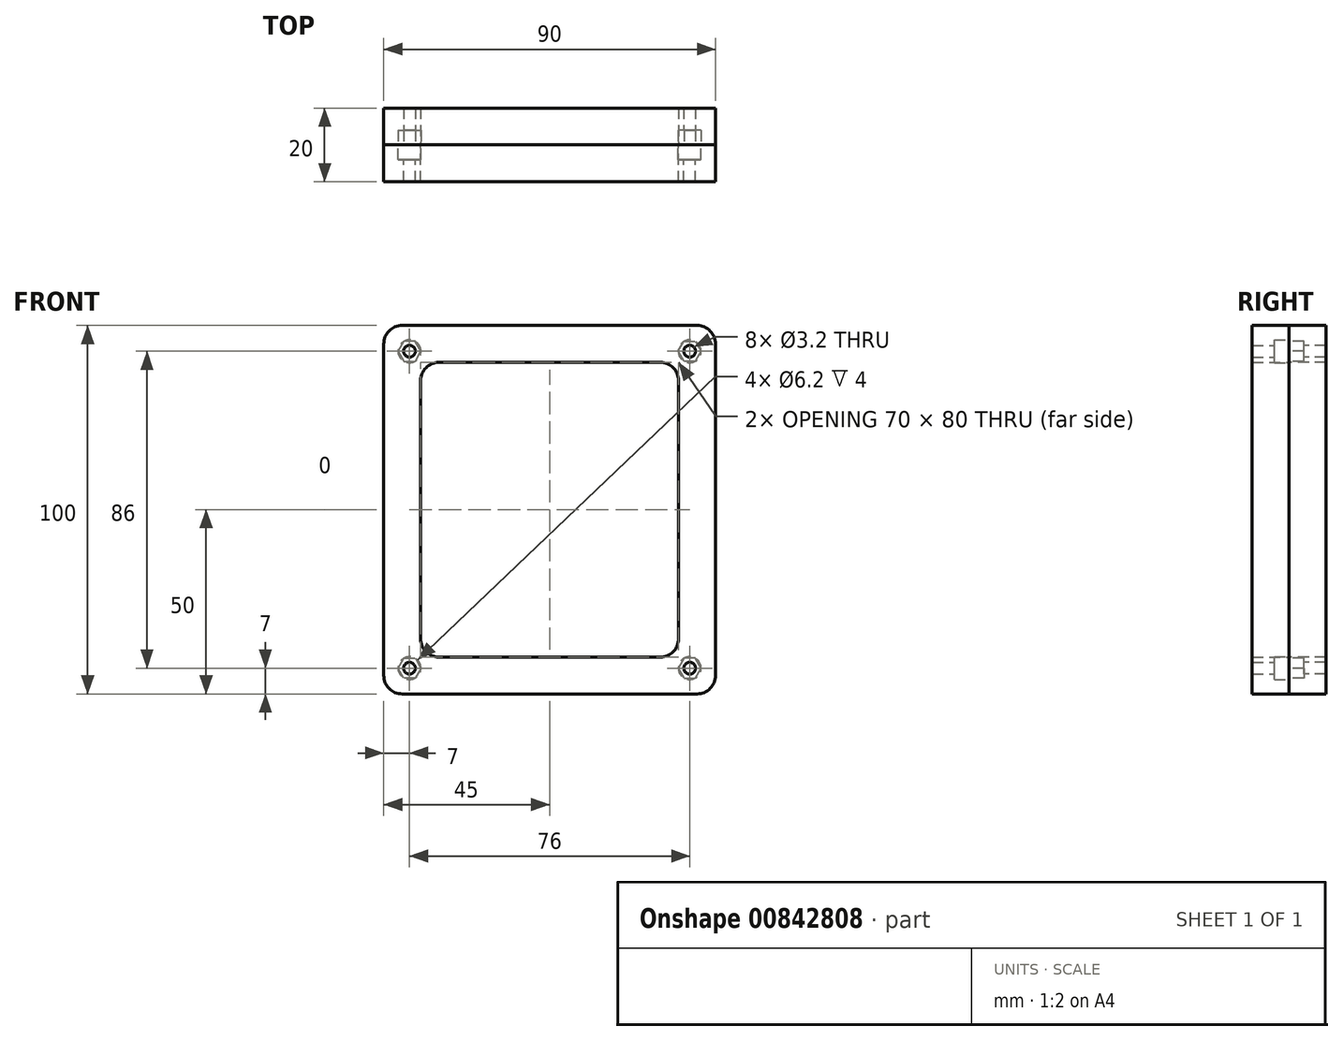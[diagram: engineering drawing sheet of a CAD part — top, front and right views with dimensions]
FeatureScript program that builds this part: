
annotation { "Feature Type Name" : "Feature", "Feature Type Description" : "" }
export const myFeature = defineFeature(function(context is Context, id is Id, definition is map)
    precondition{}
    {
        {
            var Q0;
            Q0=qCreatedBy(makeId("Front.planeOp"),FACE);
            var sketch = newSketch(context, id + "F0", { "sketchPlane" : qUnion([Q0])});
            skLineSegment(sketch, "E0.bottom", {"start": v(30, -40) * mm, "end": v(-30, -40) * mm});
            skLineSegment(sketch, "E0.top", {"start": v(30, 40) * mm, "end": v(-30, 40) * mm});
            skLineSegment(sketch, "E0.left", {"start": v(35, -35) * mm, "end": v(35, 35) * mm});
            skLineSegment(sketch, "E0.right", {"start": v(-35, -35) * mm, "end": v(-35, 35) * mm});
            skPoint(sketch, "E0.middle", {"position": v(0, 0) * mm});
            skLineSegment(sketch, "E1.bottom", {"start": v(40, -50) * mm, "end": v(-40, -50) * mm});
            skLineSegment(sketch, "E1.top", {"start": v(40, 50) * mm, "end": v(-40, 50) * mm});
            skLineSegment(sketch, "E1.left", {"start": v(45, -45) * mm, "end": v(45, 45) * mm});
            skLineSegment(sketch, "E1.right", {"start": v(-45, -45) * mm, "end": v(-45, 45) * mm});
            skLineSegment(sketch, "E2.bottom", {"start": v(10, 65) * mm, "end": v(-10, 65) * mm});
            skLineSegment(sketch, "E2.top", {"start": v(10, 75) * mm, "end": v(-10, 75) * mm});
            skLineSegment(sketch, "E2.left", {"start": v(10, 65) * mm, "end": v(10, 75) * mm});
            skLineSegment(sketch, "E2.right", {"start": v(-10, 65) * mm, "end": v(-10, 75) * mm});
            skPoint(sketch, "E2.middle", {"position": v(0, 70) * mm});
            skLineSegment(sketch, "E3", {"start": v(0, 26.34) * mm, "end": v(0, -22.9) * mm, "construction": true});
            skLineSegment(sketch, "E4", {"start": v(-20.89, 0) * mm, "end": v(22.35, 0) * mm, "construction": true});
            skCircle(sketch, "E5", {"center": v(38, 43) * mm, "radius": 1.6 * mm});
            skCircle(sketch, "E6", {"center": v(38, 43) * mm, "radius": 3.1 * mm});
            skCircle(sketch, "E7.cCircle", {"center": v(38, 43) * mm, "radius": 3.1 * mm, "construction": true});
            skLineSegment(sketch, "E7.0", {"start": v(39.55, 40.32) * mm, "end": v(36.45, 40.32) * mm});
            skLineSegment(sketch, "E7.1", {"start": v(36.45, 40.32) * mm, "end": v(34.9, 43) * mm});
            skLineSegment(sketch, "E7.2", {"start": v(34.9, 43) * mm, "end": v(36.45, 45.68) * mm});
            skLineSegment(sketch, "E7.3", {"start": v(36.45, 45.68) * mm, "end": v(39.55, 45.68) * mm});
            skLineSegment(sketch, "E7.4", {"start": v(39.55, 45.68) * mm, "end": v(41.1, 43) * mm});
            skLineSegment(sketch, "E7.5", {"start": v(41.1, 43) * mm, "end": v(39.55, 40.32) * mm});
            skLineSegment(sketch, "E8.MirrorCS", {"start": v(-34.9, 43) * mm, "end": v(-36.45, 45.68) * mm});
            skLineSegment(sketch, "E9.MirrorCS", {"start": v(-39.55, 45.68) * mm, "end": v(-41.1, 43) * mm});
            skLineSegment(sketch, "E10.MirrorCS", {"start": v(-36.45, 40.32) * mm, "end": v(-34.9, 43) * mm});
            skLineSegment(sketch, "E11.MirrorCS", {"start": v(-41.1, 43) * mm, "end": v(-39.55, 40.32) * mm});
            skLineSegment(sketch, "E12.MirrorCS", {"start": v(-36.45, 45.68) * mm, "end": v(-39.55, 45.68) * mm});
            skCircle(sketch, "E13.MirrorC", {"center": v(-38, 43) * mm, "radius": 3.1 * mm});
            skLineSegment(sketch, "E14.MirrorCS", {"start": v(-39.55, 40.32) * mm, "end": v(-36.45, 40.32) * mm});
            skCircle(sketch, "E15.MirrorC", {"center": v(-38, 43) * mm, "radius": 3.1 * mm, "construction": true});
            skCircle(sketch, "E16.MirrorC", {"center": v(-38, 43) * mm, "radius": 1.6 * mm});
            skLineSegment(sketch, "E17.MirrorCS", {"start": v(-36.45, -40.32) * mm, "end": v(-34.9, -43) * mm});
            skLineSegment(sketch, "E18.MirrorCS", {"start": v(-34.9, -43) * mm, "end": v(-36.45, -45.68) * mm});
            skLineSegment(sketch, "E19.MirrorCS", {"start": v(-39.55, -45.68) * mm, "end": v(-41.1, -43) * mm});
            skLineSegment(sketch, "E20.MirrorCS", {"start": v(-39.55, -40.32) * mm, "end": v(-36.45, -40.32) * mm});
            skLineSegment(sketch, "E21.MirrorCS", {"start": v(-41.1, -43) * mm, "end": v(-39.55, -40.32) * mm});
            skCircle(sketch, "E22.MirrorC", {"center": v(-38, -43) * mm, "radius": 3.1 * mm});
            skCircle(sketch, "E23.MirrorC", {"center": v(-38, -43) * mm, "radius": 3.1 * mm, "construction": true});
            skLineSegment(sketch, "E24.MirrorCS", {"start": v(-36.45, -45.68) * mm, "end": v(-39.55, -45.68) * mm});
            skCircle(sketch, "E25.MirrorC", {"center": v(-38, -43) * mm, "radius": 1.6 * mm});
            skLineSegment(sketch, "E26.MirrorCS", {"start": v(39.55, -40.32) * mm, "end": v(36.45, -40.32) * mm});
            skLineSegment(sketch, "E27.MirrorCS", {"start": v(36.45, -40.32) * mm, "end": v(34.9, -43) * mm});
            skLineSegment(sketch, "E28.MirrorCS", {"start": v(34.9, -43) * mm, "end": v(36.45, -45.68) * mm});
            skLineSegment(sketch, "E29.MirrorCS", {"start": v(36.45, -45.68) * mm, "end": v(39.55, -45.68) * mm});
            skLineSegment(sketch, "E30.MirrorCS", {"start": v(41.1, -43) * mm, "end": v(39.55, -40.32) * mm});
            skLineSegment(sketch, "E31.MirrorCS", {"start": v(39.55, -45.68) * mm, "end": v(41.1, -43) * mm});
            skCircle(sketch, "E32.MirrorC", {"center": v(38, -43) * mm, "radius": 3.1 * mm});
            skCircle(sketch, "E33.MirrorC", {"center": v(38, -43) * mm, "radius": 1.6 * mm});
            skCircle(sketch, "E34.MirrorC", {"center": v(38, -43) * mm, "radius": 3.1 * mm, "construction": true});
            skPoint(sketch, "E35.visualSharp", {"position": v(-35, 40) * mm});
            skArc(sketch, "E35.filletArc", {"start": v(-30, 40) * mm, "mid": v(-33.54, 38.54) * mm, "end": v(-35, 35) * mm});
            skPoint(sketch, "E36.visualSharp", {"position": v(35, 40) * mm});
            skArc(sketch, "E36.filletArc", {"start": v(35, 35) * mm, "mid": v(33.54, 38.54) * mm, "end": v(30, 40) * mm});
            skPoint(sketch, "E37.visualSharp", {"position": v(35, -40) * mm});
            skArc(sketch, "E37.filletArc", {"start": v(30, -40) * mm, "mid": v(33.54, -38.54) * mm, "end": v(35, -35) * mm});
            skPoint(sketch, "E38.visualSharp", {"position": v(-35, -40) * mm});
            skArc(sketch, "E38.filletArc", {"start": v(-35, -35) * mm, "mid": v(-33.54, -38.54) * mm, "end": v(-30, -40) * mm});
            skPoint(sketch, "E39.visualSharp", {"position": v(45, 50) * mm});
            skArc(sketch, "E39.filletArc", {"start": v(45, 45) * mm, "mid": v(43.54, 48.54) * mm, "end": v(40, 50) * mm});
            skPoint(sketch, "E40.visualSharp", {"position": v(-45, 50) * mm});
            skArc(sketch, "E40.filletArc", {"start": v(-40, 50) * mm, "mid": v(-43.54, 48.54) * mm, "end": v(-45, 45) * mm});
            skPoint(sketch, "E41.visualSharp", {"position": v(-45, -50) * mm});
            skArc(sketch, "E41.filletArc", {"start": v(-45, -45) * mm, "mid": v(-43.54, -48.54) * mm, "end": v(-40, -50) * mm});
            skPoint(sketch, "E42.visualSharp", {"position": v(45, -50) * mm});
            skArc(sketch, "E42.filletArc", {"start": v(40, -50) * mm, "mid": v(43.54, -48.54) * mm, "end": v(45, -45) * mm});
            skSolve(sketch);
        }
        {
            var Q0;
            Q0=makeQuery(id+"F0.imprint","IMPRINT",FACE,{"disambiguationData":[TD([[makeQuery(id+"F0.imprint","IMPRINT",EDGE,{"derivedFrom":sQuery(id+"F0.wireOp",EDGE,"E0.bottom")}),1.0]])]});
            var Q1;
            {var subQ0=sQuery(id+"F0.wireOp",EDGE,"E10.MirrorCS");Q1=makeQuery(id+"F0.imprint","IMPRINT",FACE,{"disambiguationData":[TD([[makeQuery(id+"F0.imprint","IMPRINT",EDGE,{"derivedFrom":subQ0}),-1.0]])]});}
            var Q2;
            Q2=makeQuery(id+"F0.imprint","IMPRINT",FACE,{"disambiguationData":[TD([[makeQuery(id+"F0.imprint","IMPRINT",EDGE,{"derivedFrom":sQuery(id+"F0.wireOp",EDGE,"E8.MirrorCS")}),1.0]])]});
            var Q3;
            {var subQ0=sQuery(id+"F0.wireOp",EDGE,"E8.MirrorCS");Q3=makeQuery(id+"F0.imprint","IMPRINT",FACE,{"disambiguationData":[TD([[makeQuery(id+"F0.imprint","IMPRINT",EDGE,{"derivedFrom":subQ0}),-1.0]])]});}
            var Q4;
            {var subQ0=sQuery(id+"F0.wireOp",EDGE,"E12.MirrorCS");Q4=makeQuery(id+"F0.imprint","IMPRINT",FACE,{"disambiguationData":[TD([[makeQuery(id+"F0.imprint","IMPRINT",EDGE,{"derivedFrom":subQ0}),-1.0]])]});}
            var Q5;
            {var subQ0=sQuery(id+"F0.wireOp",EDGE,"E9.MirrorCS");Q5=makeQuery(id+"F0.imprint","IMPRINT",FACE,{"disambiguationData":[TD([[makeQuery(id+"F0.imprint","IMPRINT",EDGE,{"derivedFrom":subQ0}),-1.0]])]});}
            var Q6;
            {var subQ0=sQuery(id+"F0.wireOp",EDGE,"E11.MirrorCS");Q6=makeQuery(id+"F0.imprint","IMPRINT",FACE,{"disambiguationData":[TD([[makeQuery(id+"F0.imprint","IMPRINT",EDGE,{"derivedFrom":subQ0}),-1.0]])]});}
            var Q7;
            {var subQ0=sQuery(id+"F0.wireOp",EDGE,"E14.MirrorCS");Q7=makeQuery(id+"F0.imprint","IMPRINT",FACE,{"disambiguationData":[TD([[makeQuery(id+"F0.imprint","IMPRINT",EDGE,{"derivedFrom":subQ0}),-1.0]])]});}
            var Q8;
            {var subQ0=sQuery(id+"F0.wireOp",EDGE,"E7.4");Q8=makeQuery(id+"F0.imprint","IMPRINT",FACE,{"disambiguationData":[TD([[makeQuery(id+"F0.imprint","IMPRINT",EDGE,{"derivedFrom":subQ0}),1.0]])]});}
            var Q9;
            Q9=makeQuery(id+"F0.imprint","IMPRINT",FACE,{"disambiguationData":[TD([[makeQuery(id+"F0.imprint","IMPRINT",EDGE,{"derivedFrom":sQuery(id+"F0.wireOp",EDGE,"E5")}),-1.0]])]});
            var Q10;
            {var subQ0=sQuery(id+"F0.wireOp",EDGE,"E7.1");Q10=makeQuery(id+"F0.imprint","IMPRINT",FACE,{"disambiguationData":[TD([[makeQuery(id+"F0.imprint","IMPRINT",EDGE,{"derivedFrom":subQ0}),1.0]])]});}
            var Q11;
            {var subQ0=sQuery(id+"F0.wireOp",EDGE,"E7.0");Q11=makeQuery(id+"F0.imprint","IMPRINT",FACE,{"disambiguationData":[TD([[makeQuery(id+"F0.imprint","IMPRINT",EDGE,{"derivedFrom":subQ0}),1.0]])]});}
            var Q12;
            {var subQ0=sQuery(id+"F0.wireOp",EDGE,"E7.3");Q12=makeQuery(id+"F0.imprint","IMPRINT",FACE,{"disambiguationData":[TD([[makeQuery(id+"F0.imprint","IMPRINT",EDGE,{"derivedFrom":subQ0}),1.0]])]});}
            var Q13;
            {var subQ0=sQuery(id+"F0.wireOp",EDGE,"E7.5");Q13=makeQuery(id+"F0.imprint","IMPRINT",FACE,{"disambiguationData":[TD([[makeQuery(id+"F0.imprint","IMPRINT",EDGE,{"derivedFrom":subQ0}),1.0]])]});}
            var Q14;
            {var subQ0=sQuery(id+"F0.wireOp",EDGE,"E7.2");Q14=makeQuery(id+"F0.imprint","IMPRINT",FACE,{"disambiguationData":[TD([[makeQuery(id+"F0.imprint","IMPRINT",EDGE,{"derivedFrom":subQ0}),1.0]])]});}
            var Q15;
            Q15=makeQuery(id+"F0.imprint","IMPRINT",FACE,{"disambiguationData":[TD([[makeQuery(id+"F0.imprint","IMPRINT",EDGE,{"derivedFrom":sQuery(id+"F0.wireOp",EDGE,"E26.MirrorCS")}),1.0]])]});
            var Q16;
            {var subQ0=sQuery(id+"F0.wireOp",EDGE,"E31.MirrorCS");Q16=makeQuery(id+"F0.imprint","IMPRINT",FACE,{"disambiguationData":[TD([[makeQuery(id+"F0.imprint","IMPRINT",EDGE,{"derivedFrom":subQ0}),-1.0]])]});}
            var Q17;
            {var subQ0=sQuery(id+"F0.wireOp",EDGE,"E27.MirrorCS");Q17=makeQuery(id+"F0.imprint","IMPRINT",FACE,{"disambiguationData":[TD([[makeQuery(id+"F0.imprint","IMPRINT",EDGE,{"derivedFrom":subQ0}),-1.0]])]});}
            var Q18;
            {var subQ0=sQuery(id+"F0.wireOp",EDGE,"E29.MirrorCS");Q18=makeQuery(id+"F0.imprint","IMPRINT",FACE,{"disambiguationData":[TD([[makeQuery(id+"F0.imprint","IMPRINT",EDGE,{"derivedFrom":subQ0}),-1.0]])]});}
            var Q19;
            {var subQ0=sQuery(id+"F0.wireOp",EDGE,"E28.MirrorCS");Q19=makeQuery(id+"F0.imprint","IMPRINT",FACE,{"disambiguationData":[TD([[makeQuery(id+"F0.imprint","IMPRINT",EDGE,{"derivedFrom":subQ0}),-1.0]])]});}
            var Q20;
            {var subQ0=sQuery(id+"F0.wireOp",EDGE,"E26.MirrorCS");Q20=makeQuery(id+"F0.imprint","IMPRINT",FACE,{"disambiguationData":[TD([[makeQuery(id+"F0.imprint","IMPRINT",EDGE,{"derivedFrom":subQ0}),-1.0]])]});}
            var Q21;
            {var subQ0=sQuery(id+"F0.wireOp",EDGE,"E30.MirrorCS");Q21=makeQuery(id+"F0.imprint","IMPRINT",FACE,{"disambiguationData":[TD([[makeQuery(id+"F0.imprint","IMPRINT",EDGE,{"derivedFrom":subQ0}),-1.0]])]});}
            var Q22;
            Q22=makeQuery(id+"F0.imprint","IMPRINT",FACE,{"disambiguationData":[TD([[makeQuery(id+"F0.imprint","IMPRINT",EDGE,{"derivedFrom":sQuery(id+"F0.wireOp",EDGE,"E17.MirrorCS")}),-1.0]])]});
            var Q23;
            {var subQ0=sQuery(id+"F0.wireOp",EDGE,"E24.MirrorCS");Q23=makeQuery(id+"F0.imprint","IMPRINT",FACE,{"disambiguationData":[TD([[makeQuery(id+"F0.imprint","IMPRINT",EDGE,{"derivedFrom":subQ0}),1.0]])]});}
            var Q24;
            {var subQ0=sQuery(id+"F0.wireOp",EDGE,"E18.MirrorCS");Q24=makeQuery(id+"F0.imprint","IMPRINT",FACE,{"disambiguationData":[TD([[makeQuery(id+"F0.imprint","IMPRINT",EDGE,{"derivedFrom":subQ0}),1.0]])]});}
            var Q25;
            {var subQ0=sQuery(id+"F0.wireOp",EDGE,"E19.MirrorCS");Q25=makeQuery(id+"F0.imprint","IMPRINT",FACE,{"disambiguationData":[TD([[makeQuery(id+"F0.imprint","IMPRINT",EDGE,{"derivedFrom":subQ0}),1.0]])]});}
            var Q26;
            {var subQ0=sQuery(id+"F0.wireOp",EDGE,"E21.MirrorCS");Q26=makeQuery(id+"F0.imprint","IMPRINT",FACE,{"disambiguationData":[TD([[makeQuery(id+"F0.imprint","IMPRINT",EDGE,{"derivedFrom":subQ0}),1.0]])]});}
            var Q27;
            {var subQ0=sQuery(id+"F0.wireOp",EDGE,"E20.MirrorCS");Q27=makeQuery(id+"F0.imprint","IMPRINT",FACE,{"disambiguationData":[TD([[makeQuery(id+"F0.imprint","IMPRINT",EDGE,{"derivedFrom":subQ0}),1.0]])]});}
            var Q28;
            {var subQ0=sQuery(id+"F0.wireOp",EDGE,"E17.MirrorCS");Q28=makeQuery(id+"F0.imprint","IMPRINT",FACE,{"disambiguationData":[TD([[makeQuery(id+"F0.imprint","IMPRINT",EDGE,{"derivedFrom":subQ0}),1.0]])]});}
            extrude(context, id + "F1", {"entities" : qUnion([Q0, Q1, Q2, Q3, Q4, Q5, Q6, Q7, Q8, Q9, Q10, Q11, Q12, Q13, Q14, Q15, Q16, Q17, Q18, Q19, Q20, Q21, Q22, Q23, Q24, Q25, Q26, Q27, Q28]), "depth" : 10 * mm, "offsetDistance" : 25 * mm});
        }
        {
            var Q0;
            Q0=makeQuery(id+"F0.imprint","IMPRINT",FACE,{"disambiguationData":[TD([[makeQuery(id+"F0.imprint","IMPRINT",EDGE,{"derivedFrom":sQuery(id+"F0.wireOp",EDGE,"E26.MirrorCS")}),1.0]])]});
            var Q1;
            Q1=makeQuery(id+"F0.imprint","IMPRINT",FACE,{"disambiguationData":[TD([[makeQuery(id+"F0.imprint","IMPRINT",EDGE,{"derivedFrom":sQuery(id+"F0.wireOp",EDGE,"E0.bottom")}),1.0]])]});
            var Q2;
            Q2=makeQuery(id+"F0.imprint","IMPRINT",FACE,{"disambiguationData":[TD([[makeQuery(id+"F0.imprint","IMPRINT",EDGE,{"derivedFrom":sQuery(id+"F0.wireOp",EDGE,"E17.MirrorCS")}),-1.0]])]});
            var Q3;
            Q3=makeQuery(id+"F0.imprint","IMPRINT",FACE,{"disambiguationData":[TD([[makeQuery(id+"F0.imprint","IMPRINT",EDGE,{"derivedFrom":sQuery(id+"F0.wireOp",EDGE,"E5")}),-1.0]])]});
            var Q4;
            Q4=makeQuery(id+"F0.imprint","IMPRINT",FACE,{"disambiguationData":[TD([[makeQuery(id+"F0.imprint","IMPRINT",EDGE,{"derivedFrom":sQuery(id+"F0.wireOp",EDGE,"E8.MirrorCS")}),1.0]])]});
            var Q5;
            {var subQ0=sQuery(id+"F0.wireOp",EDGE,"E14.MirrorCS");Q5=makeQuery(id+"F0.imprint","IMPRINT",FACE,{"disambiguationData":[TD([[makeQuery(id+"F0.imprint","IMPRINT",EDGE,{"derivedFrom":subQ0}),-1.0]])]});}
            var Q6;
            {var subQ0=sQuery(id+"F0.wireOp",EDGE,"E11.MirrorCS");Q6=makeQuery(id+"F0.imprint","IMPRINT",FACE,{"disambiguationData":[TD([[makeQuery(id+"F0.imprint","IMPRINT",EDGE,{"derivedFrom":subQ0}),-1.0]])]});}
            var Q7;
            {var subQ0=sQuery(id+"F0.wireOp",EDGE,"E28.MirrorCS");Q7=makeQuery(id+"F0.imprint","IMPRINT",FACE,{"disambiguationData":[TD([[makeQuery(id+"F0.imprint","IMPRINT",EDGE,{"derivedFrom":subQ0}),-1.0]])]});}
            var Q8;
            {var subQ0=sQuery(id+"F0.wireOp",EDGE,"E7.2");Q8=makeQuery(id+"F0.imprint","IMPRINT",FACE,{"disambiguationData":[TD([[makeQuery(id+"F0.imprint","IMPRINT",EDGE,{"derivedFrom":subQ0}),1.0]])]});}
            var Q9;
            {var subQ0=sQuery(id+"F0.wireOp",EDGE,"E21.MirrorCS");Q9=makeQuery(id+"F0.imprint","IMPRINT",FACE,{"disambiguationData":[TD([[makeQuery(id+"F0.imprint","IMPRINT",EDGE,{"derivedFrom":subQ0}),1.0]])]});}
            var Q10;
            {var subQ0=sQuery(id+"F0.wireOp",EDGE,"E7.0");Q10=makeQuery(id+"F0.imprint","IMPRINT",FACE,{"disambiguationData":[TD([[makeQuery(id+"F0.imprint","IMPRINT",EDGE,{"derivedFrom":subQ0}),1.0]])]});}
            var Q11;
            {var subQ0=sQuery(id+"F0.wireOp",EDGE,"E9.MirrorCS");Q11=makeQuery(id+"F0.imprint","IMPRINT",FACE,{"disambiguationData":[TD([[makeQuery(id+"F0.imprint","IMPRINT",EDGE,{"derivedFrom":subQ0}),-1.0]])]});}
            var Q12;
            {var subQ0=sQuery(id+"F0.wireOp",EDGE,"E7.3");Q12=makeQuery(id+"F0.imprint","IMPRINT",FACE,{"disambiguationData":[TD([[makeQuery(id+"F0.imprint","IMPRINT",EDGE,{"derivedFrom":subQ0}),1.0]])]});}
            var Q13;
            {var subQ0=sQuery(id+"F0.wireOp",EDGE,"E29.MirrorCS");Q13=makeQuery(id+"F0.imprint","IMPRINT",FACE,{"disambiguationData":[TD([[makeQuery(id+"F0.imprint","IMPRINT",EDGE,{"derivedFrom":subQ0}),-1.0]])]});}
            var Q14;
            {var subQ0=sQuery(id+"F0.wireOp",EDGE,"E12.MirrorCS");Q14=makeQuery(id+"F0.imprint","IMPRINT",FACE,{"disambiguationData":[TD([[makeQuery(id+"F0.imprint","IMPRINT",EDGE,{"derivedFrom":subQ0}),-1.0]])]});}
            var Q15;
            {var subQ0=sQuery(id+"F0.wireOp",EDGE,"E26.MirrorCS");Q15=makeQuery(id+"F0.imprint","IMPRINT",FACE,{"disambiguationData":[TD([[makeQuery(id+"F0.imprint","IMPRINT",EDGE,{"derivedFrom":subQ0}),-1.0]])]});}
            var Q16;
            {var subQ0=sQuery(id+"F0.wireOp",EDGE,"E24.MirrorCS");Q16=makeQuery(id+"F0.imprint","IMPRINT",FACE,{"disambiguationData":[TD([[makeQuery(id+"F0.imprint","IMPRINT",EDGE,{"derivedFrom":subQ0}),1.0]])]});}
            var Q17;
            {var subQ0=sQuery(id+"F0.wireOp",EDGE,"E7.4");Q17=makeQuery(id+"F0.imprint","IMPRINT",FACE,{"disambiguationData":[TD([[makeQuery(id+"F0.imprint","IMPRINT",EDGE,{"derivedFrom":subQ0}),1.0]])]});}
            var Q18;
            {var subQ0=sQuery(id+"F0.wireOp",EDGE,"E7.1");Q18=makeQuery(id+"F0.imprint","IMPRINT",FACE,{"disambiguationData":[TD([[makeQuery(id+"F0.imprint","IMPRINT",EDGE,{"derivedFrom":subQ0}),1.0]])]});}
            var Q19;
            {var subQ0=sQuery(id+"F0.wireOp",EDGE,"E19.MirrorCS");Q19=makeQuery(id+"F0.imprint","IMPRINT",FACE,{"disambiguationData":[TD([[makeQuery(id+"F0.imprint","IMPRINT",EDGE,{"derivedFrom":subQ0}),1.0]])]});}
            var Q20;
            {var subQ0=sQuery(id+"F0.wireOp",EDGE,"E7.5");Q20=makeQuery(id+"F0.imprint","IMPRINT",FACE,{"disambiguationData":[TD([[makeQuery(id+"F0.imprint","IMPRINT",EDGE,{"derivedFrom":subQ0}),1.0]])]});}
            var Q21;
            {var subQ0=sQuery(id+"F0.wireOp",EDGE,"E31.MirrorCS");Q21=makeQuery(id+"F0.imprint","IMPRINT",FACE,{"disambiguationData":[TD([[makeQuery(id+"F0.imprint","IMPRINT",EDGE,{"derivedFrom":subQ0}),-1.0]])]});}
            var Q22;
            {var subQ0=sQuery(id+"F0.wireOp",EDGE,"E18.MirrorCS");Q22=makeQuery(id+"F0.imprint","IMPRINT",FACE,{"disambiguationData":[TD([[makeQuery(id+"F0.imprint","IMPRINT",EDGE,{"derivedFrom":subQ0}),1.0]])]});}
            var Q23;
            {var subQ0=sQuery(id+"F0.wireOp",EDGE,"E10.MirrorCS");Q23=makeQuery(id+"F0.imprint","IMPRINT",FACE,{"disambiguationData":[TD([[makeQuery(id+"F0.imprint","IMPRINT",EDGE,{"derivedFrom":subQ0}),-1.0]])]});}
            var Q24;
            {var subQ0=sQuery(id+"F0.wireOp",EDGE,"E17.MirrorCS");Q24=makeQuery(id+"F0.imprint","IMPRINT",FACE,{"disambiguationData":[TD([[makeQuery(id+"F0.imprint","IMPRINT",EDGE,{"derivedFrom":subQ0}),1.0]])]});}
            var Q25;
            {var subQ0=sQuery(id+"F0.wireOp",EDGE,"E30.MirrorCS");Q25=makeQuery(id+"F0.imprint","IMPRINT",FACE,{"disambiguationData":[TD([[makeQuery(id+"F0.imprint","IMPRINT",EDGE,{"derivedFrom":subQ0}),-1.0]])]});}
            var Q26;
            {var subQ0=sQuery(id+"F0.wireOp",EDGE,"E8.MirrorCS");Q26=makeQuery(id+"F0.imprint","IMPRINT",FACE,{"disambiguationData":[TD([[makeQuery(id+"F0.imprint","IMPRINT",EDGE,{"derivedFrom":subQ0}),-1.0]])]});}
            var Q27;
            {var subQ0=sQuery(id+"F0.wireOp",EDGE,"E20.MirrorCS");Q27=makeQuery(id+"F0.imprint","IMPRINT",FACE,{"disambiguationData":[TD([[makeQuery(id+"F0.imprint","IMPRINT",EDGE,{"derivedFrom":subQ0}),1.0]])]});}
            var Q28;
            {var subQ0=sQuery(id+"F0.wireOp",EDGE,"E27.MirrorCS");Q28=makeQuery(id+"F0.imprint","IMPRINT",FACE,{"disambiguationData":[TD([[makeQuery(id+"F0.imprint","IMPRINT",EDGE,{"derivedFrom":subQ0}),-1.0]])]});}
            extrude(context, id + "F2", {"entities" : qUnion([Q0, Q1, Q2, Q3, Q4, Q5, Q6, Q7, Q8, Q9, Q10, Q11, Q12, Q13, Q14, Q15, Q16, Q17, Q18, Q19, Q20, Q21, Q22, Q23, Q24, Q25, Q26, Q27, Q28]), "oppositeDirection" : true, "depth" : 10 * mm, "offsetDistance" : 25 * mm});
        }
        {
            assignVariable(context, id + "F3", {"variableType" : VariableType.LENGTH, "name" : "Relief", "lengthValue" : 4 * mm});
        }
        {
            var Q0;
            Q0=makeQuery(id+"F0.imprint","IMPRINT",FACE,{"disambiguationData":[TD([[makeQuery(id+"F0.imprint","IMPRINT",EDGE,{"derivedFrom":sQuery(id+"F0.wireOp",EDGE,"E26.MirrorCS")}),1.0]])]});
            var Q1;
            Q1=makeQuery(id+"F0.imprint","IMPRINT",FACE,{"disambiguationData":[TD([[makeQuery(id+"F0.imprint","IMPRINT",EDGE,{"derivedFrom":sQuery(id+"F0.wireOp",EDGE,"E17.MirrorCS")}),-1.0]])]});
            var Q2;
            Q2=makeQuery(id+"F0.imprint","IMPRINT",FACE,{"disambiguationData":[TD([[makeQuery(id+"F0.imprint","IMPRINT",EDGE,{"derivedFrom":sQuery(id+"F0.wireOp",EDGE,"E8.MirrorCS")}),1.0]])]});
            var Q3;
            Q3=makeQuery(id+"F0.imprint","IMPRINT",FACE,{"disambiguationData":[TD([[makeQuery(id+"F0.imprint","IMPRINT",EDGE,{"derivedFrom":sQuery(id+"F0.wireOp",EDGE,"E5")}),-1.0]])]});
            extrude(context, id + "F4", {"entities" : qUnion([Q0, Q1, Q2, Q3]), "operationType" : NewBodyOperationType.REMOVE, "oppositeDirection" : true, "depth" : getVariable(context, 'Relief'), "offsetDistance" : 25 * mm});
        }
        {
            var Q0;
            Q0=makeQuery(id+"F0.imprint","IMPRINT",FACE,{"disambiguationData":[TD([[makeQuery(id+"F0.imprint","IMPRINT",EDGE,{"derivedFrom":sQuery(id+"F0.wireOp",EDGE,"E26.MirrorCS")}),1.0]])]});
            var Q1;
            {var subQ0=sQuery(id+"F0.wireOp",EDGE,"E26.MirrorCS");Q1=makeQuery(id+"F0.imprint","IMPRINT",FACE,{"disambiguationData":[TD([[makeQuery(id+"F0.imprint","IMPRINT",EDGE,{"derivedFrom":subQ0}),-1.0]])]});}
            var Q2;
            {var subQ0=sQuery(id+"F0.wireOp",EDGE,"E30.MirrorCS");Q2=makeQuery(id+"F0.imprint","IMPRINT",FACE,{"disambiguationData":[TD([[makeQuery(id+"F0.imprint","IMPRINT",EDGE,{"derivedFrom":subQ0}),-1.0]])]});}
            var Q3;
            {var subQ0=sQuery(id+"F0.wireOp",EDGE,"E31.MirrorCS");Q3=makeQuery(id+"F0.imprint","IMPRINT",FACE,{"disambiguationData":[TD([[makeQuery(id+"F0.imprint","IMPRINT",EDGE,{"derivedFrom":subQ0}),-1.0]])]});}
            var Q4;
            {var subQ0=sQuery(id+"F0.wireOp",EDGE,"E29.MirrorCS");Q4=makeQuery(id+"F0.imprint","IMPRINT",FACE,{"disambiguationData":[TD([[makeQuery(id+"F0.imprint","IMPRINT",EDGE,{"derivedFrom":subQ0}),-1.0]])]});}
            var Q5;
            {var subQ0=sQuery(id+"F0.wireOp",EDGE,"E28.MirrorCS");Q5=makeQuery(id+"F0.imprint","IMPRINT",FACE,{"disambiguationData":[TD([[makeQuery(id+"F0.imprint","IMPRINT",EDGE,{"derivedFrom":subQ0}),-1.0]])]});}
            var Q6;
            {var subQ0=sQuery(id+"F0.wireOp",EDGE,"E27.MirrorCS");Q6=makeQuery(id+"F0.imprint","IMPRINT",FACE,{"disambiguationData":[TD([[makeQuery(id+"F0.imprint","IMPRINT",EDGE,{"derivedFrom":subQ0}),-1.0]])]});}
            var Q7;
            {var subQ0=sQuery(id+"F0.wireOp",EDGE,"E19.MirrorCS");Q7=makeQuery(id+"F0.imprint","IMPRINT",FACE,{"disambiguationData":[TD([[makeQuery(id+"F0.imprint","IMPRINT",EDGE,{"derivedFrom":subQ0}),1.0]])]});}
            var Q8;
            {var subQ0=sQuery(id+"F0.wireOp",EDGE,"E24.MirrorCS");Q8=makeQuery(id+"F0.imprint","IMPRINT",FACE,{"disambiguationData":[TD([[makeQuery(id+"F0.imprint","IMPRINT",EDGE,{"derivedFrom":subQ0}),1.0]])]});}
            var Q9;
            {var subQ0=sQuery(id+"F0.wireOp",EDGE,"E18.MirrorCS");Q9=makeQuery(id+"F0.imprint","IMPRINT",FACE,{"disambiguationData":[TD([[makeQuery(id+"F0.imprint","IMPRINT",EDGE,{"derivedFrom":subQ0}),1.0]])]});}
            var Q10;
            {var subQ0=sQuery(id+"F0.wireOp",EDGE,"E17.MirrorCS");Q10=makeQuery(id+"F0.imprint","IMPRINT",FACE,{"disambiguationData":[TD([[makeQuery(id+"F0.imprint","IMPRINT",EDGE,{"derivedFrom":subQ0}),1.0]])]});}
            var Q11;
            {var subQ0=sQuery(id+"F0.wireOp",EDGE,"E20.MirrorCS");Q11=makeQuery(id+"F0.imprint","IMPRINT",FACE,{"disambiguationData":[TD([[makeQuery(id+"F0.imprint","IMPRINT",EDGE,{"derivedFrom":subQ0}),1.0]])]});}
            var Q12;
            {var subQ0=sQuery(id+"F0.wireOp",EDGE,"E21.MirrorCS");Q12=makeQuery(id+"F0.imprint","IMPRINT",FACE,{"disambiguationData":[TD([[makeQuery(id+"F0.imprint","IMPRINT",EDGE,{"derivedFrom":subQ0}),1.0]])]});}
            var Q13;
            Q13=makeQuery(id+"F0.imprint","IMPRINT",FACE,{"disambiguationData":[TD([[makeQuery(id+"F0.imprint","IMPRINT",EDGE,{"derivedFrom":sQuery(id+"F0.wireOp",EDGE,"E17.MirrorCS")}),-1.0]])]});
            var Q14;
            {var subQ0=sQuery(id+"F0.wireOp",EDGE,"E14.MirrorCS");Q14=makeQuery(id+"F0.imprint","IMPRINT",FACE,{"disambiguationData":[TD([[makeQuery(id+"F0.imprint","IMPRINT",EDGE,{"derivedFrom":subQ0}),-1.0]])]});}
            var Q15;
            {var subQ0=sQuery(id+"F0.wireOp",EDGE,"E10.MirrorCS");Q15=makeQuery(id+"F0.imprint","IMPRINT",FACE,{"disambiguationData":[TD([[makeQuery(id+"F0.imprint","IMPRINT",EDGE,{"derivedFrom":subQ0}),-1.0]])]});}
            var Q16;
            {var subQ0=sQuery(id+"F0.wireOp",EDGE,"E8.MirrorCS");Q16=makeQuery(id+"F0.imprint","IMPRINT",FACE,{"disambiguationData":[TD([[makeQuery(id+"F0.imprint","IMPRINT",EDGE,{"derivedFrom":subQ0}),-1.0]])]});}
            var Q17;
            {var subQ0=sQuery(id+"F0.wireOp",EDGE,"E12.MirrorCS");Q17=makeQuery(id+"F0.imprint","IMPRINT",FACE,{"disambiguationData":[TD([[makeQuery(id+"F0.imprint","IMPRINT",EDGE,{"derivedFrom":subQ0}),-1.0]])]});}
            var Q18;
            {var subQ0=sQuery(id+"F0.wireOp",EDGE,"E9.MirrorCS");Q18=makeQuery(id+"F0.imprint","IMPRINT",FACE,{"disambiguationData":[TD([[makeQuery(id+"F0.imprint","IMPRINT",EDGE,{"derivedFrom":subQ0}),-1.0]])]});}
            var Q19;
            {var subQ0=sQuery(id+"F0.wireOp",EDGE,"E11.MirrorCS");Q19=makeQuery(id+"F0.imprint","IMPRINT",FACE,{"disambiguationData":[TD([[makeQuery(id+"F0.imprint","IMPRINT",EDGE,{"derivedFrom":subQ0}),-1.0]])]});}
            var Q20;
            Q20=makeQuery(id+"F0.imprint","IMPRINT",FACE,{"disambiguationData":[TD([[makeQuery(id+"F0.imprint","IMPRINT",EDGE,{"derivedFrom":sQuery(id+"F0.wireOp",EDGE,"E8.MirrorCS")}),1.0]])]});
            var Q21;
            {var subQ0=sQuery(id+"F0.wireOp",EDGE,"E7.1");Q21=makeQuery(id+"F0.imprint","IMPRINT",FACE,{"disambiguationData":[TD([[makeQuery(id+"F0.imprint","IMPRINT",EDGE,{"derivedFrom":subQ0}),1.0]])]});}
            var Q22;
            {var subQ0=sQuery(id+"F0.wireOp",EDGE,"E7.0");Q22=makeQuery(id+"F0.imprint","IMPRINT",FACE,{"disambiguationData":[TD([[makeQuery(id+"F0.imprint","IMPRINT",EDGE,{"derivedFrom":subQ0}),1.0]])]});}
            var Q23;
            {var subQ0=sQuery(id+"F0.wireOp",EDGE,"E7.5");Q23=makeQuery(id+"F0.imprint","IMPRINT",FACE,{"disambiguationData":[TD([[makeQuery(id+"F0.imprint","IMPRINT",EDGE,{"derivedFrom":subQ0}),1.0]])]});}
            var Q24;
            {var subQ0=sQuery(id+"F0.wireOp",EDGE,"E7.4");Q24=makeQuery(id+"F0.imprint","IMPRINT",FACE,{"disambiguationData":[TD([[makeQuery(id+"F0.imprint","IMPRINT",EDGE,{"derivedFrom":subQ0}),1.0]])]});}
            var Q25;
            {var subQ0=sQuery(id+"F0.wireOp",EDGE,"E7.3");Q25=makeQuery(id+"F0.imprint","IMPRINT",FACE,{"disambiguationData":[TD([[makeQuery(id+"F0.imprint","IMPRINT",EDGE,{"derivedFrom":subQ0}),1.0]])]});}
            var Q26;
            {var subQ0=sQuery(id+"F0.wireOp",EDGE,"E7.2");Q26=makeQuery(id+"F0.imprint","IMPRINT",FACE,{"disambiguationData":[TD([[makeQuery(id+"F0.imprint","IMPRINT",EDGE,{"derivedFrom":subQ0}),1.0]])]});}
            var Q27;
            Q27=makeQuery(id+"F0.imprint","IMPRINT",FACE,{"disambiguationData":[TD([[makeQuery(id+"F0.imprint","IMPRINT",EDGE,{"derivedFrom":sQuery(id+"F0.wireOp",EDGE,"E5")}),-1.0]])]});
            extrude(context, id + "F5", {"entities" : qUnion([Q0, Q1, Q2, Q3, Q4, Q5, Q6, Q7, Q8, Q9, Q10, Q11, Q12, Q13, Q14, Q15, Q16, Q17, Q18, Q19, Q20, Q21, Q22, Q23, Q24, Q25, Q26, Q27]), "operationType" : NewBodyOperationType.REMOVE, "depth" : getVariable(context, 'Relief'), "offsetDistance" : 25 * mm});
        }
    });
